# Revit family: НЕВАТОМ_Вентилятор VKK 355m, версия 1
name_source: partatom
category: Оборудование
revit_build: Autodesk Revit 2017 (Build: 20170118_1100(x64)
units: mm (PartAtom-declared; Revit-internal decimal feet)

## family parameters
Всегда вертикально = Да
На основе рабочей плоскости = Нет
Общий = Нет
При загрузке вырезать с полостями = Нет
Размер круглого соединителя = Использовать диаметр
Тип детали = Вставляется
Точка расчета площади = Нет

## types (2) — shared parameters
ADSK_Единица измерения = шт.
ADSK_Завод-изготовитель = НЕВАТОМ
ADSK_Количество = 1
ADSK_Масса = 14
ADSK_Масса_Текст = 14
ADSK_Материал наименование = Оцинкованная сталь
ADSK_Наименование = Вентилятор канальный круглый
ADSK_Полная мощность = 0 кВт
ADSK_Размер_Высота = 562 мм
ADSK_Размер_Длина = 512 мм
ADSK_Размер_Ширина = 426 мм
B = 566 мм
C = 540 мм
D = 512 мм
E = 110 мм
F = 107 мм
H = 562 мм
L = 426 мм
Nevatom_URL = https://t.me
d = 353 мм
h = 50 мм
Ключевая пометка = Вентиляция
Корпус = Резина
Материал = Сталь серая

## per-type parameters (varying)
| type | ADSK_Напряжение | ADSK_Ток | ADSK_Частота вращения вентилятора | Макс. расход воздуха | Полное давление |
| VKK - 355 - 4E m | 230 В | 1 А | 1360 | 2000.0 м³/ч | 400.0 Па |
| VKK - 355 - 4D m | 380 В | 0 А | 1380 | 2350.0 м³/ч | 270.0 Па |

note: column(s) folded — value = type name in every type: ADSK_Марка
